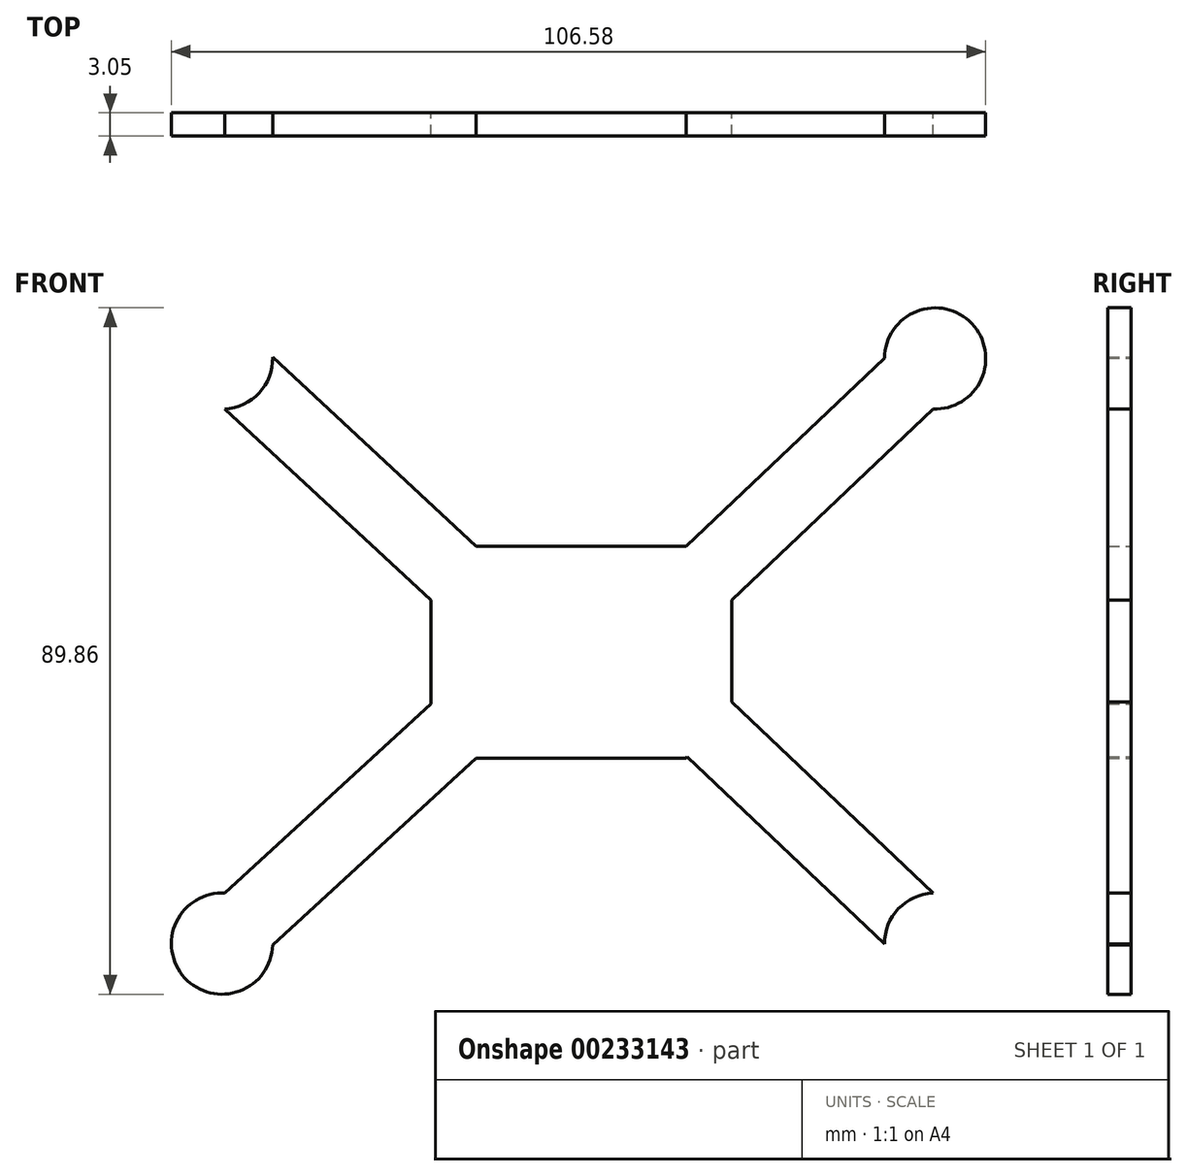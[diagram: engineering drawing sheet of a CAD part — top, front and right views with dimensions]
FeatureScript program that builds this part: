
annotation { "Feature Type Name" : "Feature", "Feature Type Description" : "" }
export const myFeature = defineFeature(function(context is Context, id is Id, definition is map)
    precondition{}
    {
        {
            var Q0;
            Q0=qCreatedBy(makeId("Front.planeOp"),FACE);
            var sketch = newSketch(context, id + "F0", { "sketchPlane" : qUnion([Q0])});
            skLineSegment(sketch, "E0", {"start": v(-13.4, 0) * mm, "end": v(14.09, 0) * mm});
            skLineSegment(sketch, "E1", {"start": v(-13.4, -27.74) * mm, "end": v(14.09, -27.74) * mm});
            skLineSegment(sketch, "E2", {"start": v(-13.4, 0) * mm, "end": v(-19.33, -7.08) * mm});
            skLineSegment(sketch, "E3", {"start": v(14.09, 0) * mm, "end": v(20.02, -7.08) * mm});
            skLineSegment(sketch, "E4", {"start": v(-13.4, -27.74) * mm, "end": v(-19.33, -20.67) * mm});
            skLineSegment(sketch, "E5", {"start": v(14.09, -27.74) * mm, "end": v(20.02, -20.67) * mm});
            skLineSegment(sketch, "E6", {"start": v(-19.33, -20.67) * mm, "end": v(-19.33, -7.08) * mm});
            skLineSegment(sketch, "E7", {"start": v(20.02, -20.67) * mm, "end": v(20.02, -7.08) * mm});
            skLineSegment(sketch, "E8", {"start": v(14.09, 0) * mm, "end": v(43.64, 28.06) * mm});
            skLineSegment(sketch, "E9", {"start": v(20.02, -7.08) * mm, "end": v(49.69, 21.08) * mm});
            skCircle(sketch, "E10", {"center": v(46.67, 24.57) * mm, "radius": 6.63 * mm});
            skCircle(sketch, "E11.MirrorC", {"center": v(-46.67, 24.57) * mm, "radius": 6.63 * mm});
            skLineSegment(sketch, "E12.MirrorCS", {"start": v(20.02, -20.4) * mm, "end": v(49.69, -48.56) * mm});
            skLineSegment(sketch, "E13.MirrorCS", {"start": v(14.09, -27.48) * mm, "end": v(43.64, -55.53) * mm});
            skCircle(sketch, "E14.MirrorC", {"center": v(46.67, -52.05) * mm, "radius": 6.63 * mm});
            skCircle(sketch, "E15.MirrorC", {"center": v(-46.67, -52.05) * mm, "radius": 6.63 * mm});
            skLineSegment(sketch, "E16", {"start": v(-43.64, 28.06) * mm, "end": v(-13.4, 0) * mm});
            skLineSegment(sketch, "E17", {"start": v(-49.69, 21.08) * mm, "end": v(-19.33, -7.08) * mm});
            skLineSegment(sketch, "E18", {"start": v(-19.33, -20.67) * mm, "end": v(-49.69, -48.56) * mm});
            skLineSegment(sketch, "E19", {"start": v(-43.64, -55.53) * mm, "end": v(-13.4, -27.74) * mm});
            skSolve(sketch);
        }
        {
            var Q0;
            {var subQ0=sQuery(id+"F0.wireOp",EDGE,"E11.MirrorC");var subQ1=makeQuery(id+"F0.imprint","INTERSECT",VERTEX,{"derivedFrom":[subQ0,sQuery(id+"F0.wireOp",EDGE,"E16")]});Q0=makeQuery(id+"F0.imprint","IMPRINT",FACE,{"disambiguationData":[TD([[makeQuery(id+"F0.imprint","IMPRINT",EDGE,{"disambiguationData":[TD([[subQ1,-1.0]])],"derivedFrom":subQ0}),-1.0]])]});}
            var Q1;
            {var subQ0=sQuery(id+"F0.wireOp",EDGE,"E2");Q1=makeQuery(id+"F0.imprint","IMPRINT",FACE,{"disambiguationData":[TD([[makeQuery(id+"F0.imprint","IMPRINT",EDGE,{"derivedFrom":subQ0}),-1.0]])]});}
            var Q2;
            Q2=makeQuery(id+"F0.imprint","IMPRINT",FACE,{"disambiguationData":[TD([[makeQuery(id+"F0.imprint","IMPRINT",EDGE,{"derivedFrom":sQuery(id+"F0.wireOp",EDGE,"E0")}),-1.0]])]});
            var Q3;
            {var subQ0=sQuery(id+"F0.wireOp",EDGE,"E3");Q3=makeQuery(id+"F0.imprint","IMPRINT",FACE,{"disambiguationData":[TD([[makeQuery(id+"F0.imprint","IMPRINT",EDGE,{"derivedFrom":subQ0}),1.0]])]});}
            var Q4;
            {var subQ0=sQuery(id+"F0.wireOp",EDGE,"E10");var subQ1=makeQuery(id+"F0.imprint","INTERSECT",VERTEX,{"derivedFrom":[sQuery(id+"F0.wireOp",EDGE,"E8"),subQ0]});Q4=makeQuery(id+"F0.imprint","IMPRINT",FACE,{"disambiguationData":[TD([[makeQuery(id+"F0.imprint","IMPRINT",EDGE,{"disambiguationData":[TD([[subQ1,-1.0]])],"derivedFrom":subQ0}),1.0]])]});}
            var Q5;
            {var subQ1=sQuery(id+"F0.wireOp",EDGE,"E5");var subQ5=sQuery(id+"F0.wireOp",EDGE,"E7");var subQ6=makeQuery(id+"F0.imprint","INTERSECT",VERTEX,{"derivedFrom":[subQ1,subQ5]});Q5=makeQuery(id+"F0.imprint","IMPRINT",FACE,{"disambiguationData":[TD([[makeQuery(id+"F0.imprint","IMPRINT",EDGE,{"disambiguationData":[TD([[subQ6,1.0]])],"derivedFrom":subQ1}),-1.0]])]});}
            var Q6;
            {var subQ0=sQuery(id+"F0.wireOp",EDGE,"E14.MirrorC");var subQ1=makeQuery(id+"F0.imprint","INTERSECT",VERTEX,{"derivedFrom":[sQuery(id+"F0.wireOp",EDGE,"E12.MirrorCS"),subQ0]});Q6=makeQuery(id+"F0.imprint","IMPRINT",FACE,{"disambiguationData":[TD([[makeQuery(id+"F0.imprint","IMPRINT",EDGE,{"disambiguationData":[TD([[subQ1,1.0]])],"derivedFrom":subQ0}),-1.0]])]});}
            var Q7;
            {var subQ0=sQuery(id+"F0.wireOp",EDGE,"E4");Q7=makeQuery(id+"F0.imprint","IMPRINT",FACE,{"disambiguationData":[TD([[makeQuery(id+"F0.imprint","IMPRINT",EDGE,{"derivedFrom":subQ0}),1.0]])]});}
            var Q8;
            {var subQ0=sQuery(id+"F0.wireOp",EDGE,"E15.MirrorC");var subQ1=makeQuery(id+"F0.imprint","INTERSECT",VERTEX,{"derivedFrom":[subQ0,sQuery(id+"F0.wireOp",EDGE,"E18")]});Q8=makeQuery(id+"F0.imprint","IMPRINT",FACE,{"disambiguationData":[TD([[makeQuery(id+"F0.imprint","IMPRINT",EDGE,{"disambiguationData":[TD([[subQ1,1.0]])],"derivedFrom":subQ0}),1.0]])]});}
            extrude(context, id + "F1", {"entities" : qUnion([Q0, Q1, Q2, Q3, Q4, Q5, Q6, Q7, Q8]), "depth" : 3.05 * mm});
        }
    });
